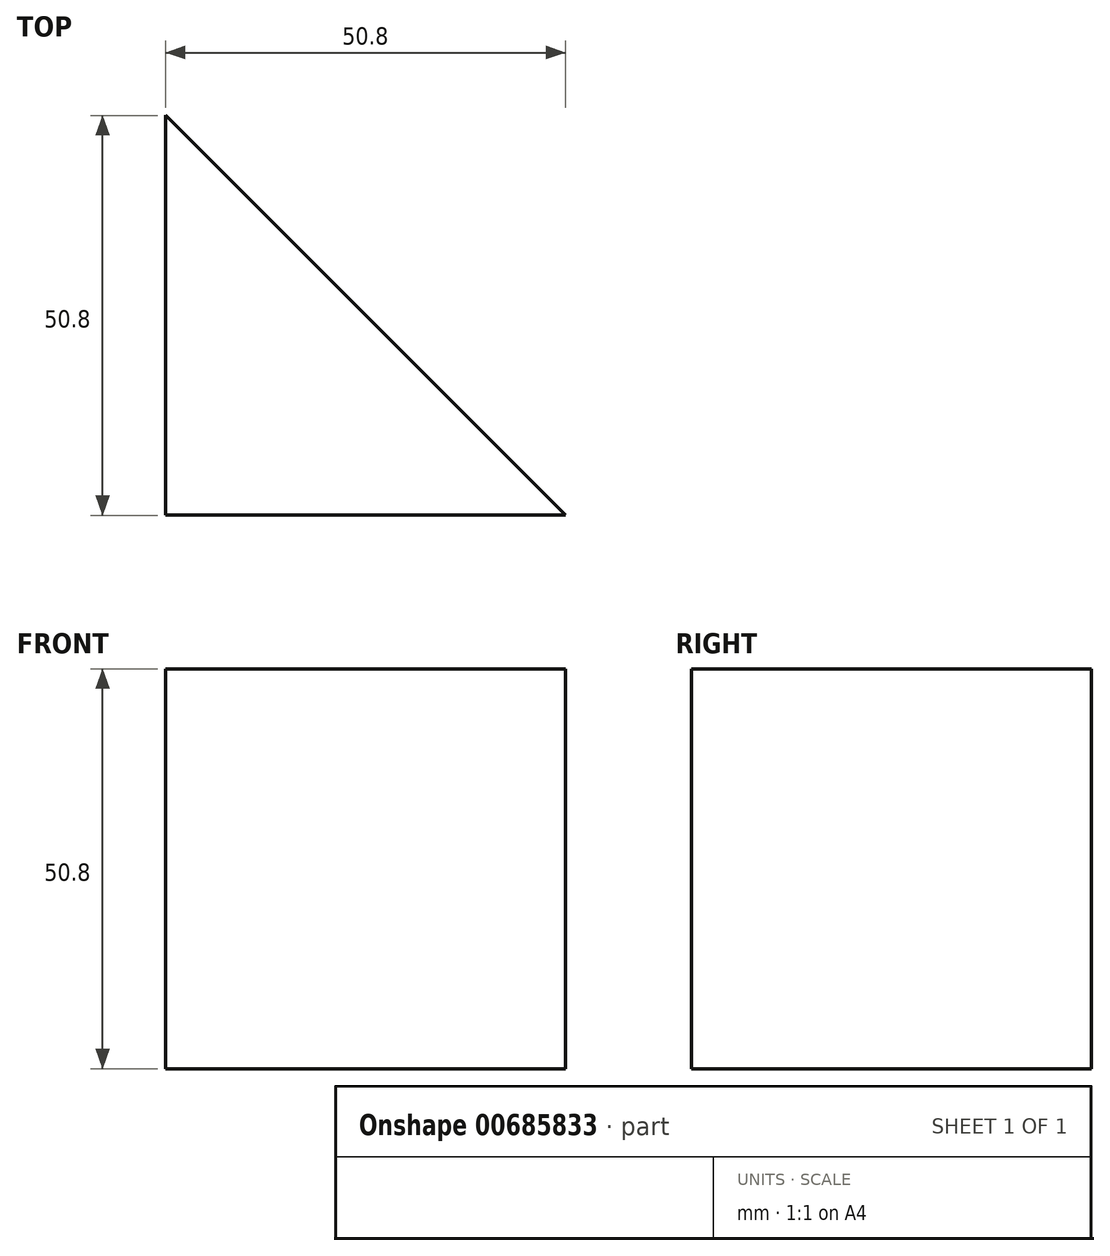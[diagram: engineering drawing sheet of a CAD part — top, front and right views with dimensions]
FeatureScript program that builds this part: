
annotation { "Feature Type Name" : "Feature", "Feature Type Description" : "" }
export const myFeature = defineFeature(function(context is Context, id is Id, definition is map)
    precondition{}
    {
        {
            var Q0;
            Q0=qCreatedBy(makeId("Top.planeOp"),FACE);
            var sketch = newSketch(context, id + "F0", { "sketchPlane" : qUnion([Q0])});
            skLineSegment(sketch, "E0.top", {"start": v(-26.26, -31.75) * mm, "end": v(24.54, -31.75) * mm});
            skLineSegment(sketch, "E0.left", {"start": v(-26.26, 19.05) * mm, "end": v(-26.26, -31.75) * mm});
            skLineSegment(sketch, "E1", {"start": v(-26.26, 19.05) * mm, "end": v(24.54, -31.75) * mm});
            skSolve(sketch);
        }
        {
            var Q0;
            Q0 = qSketchRegion(id + "F0", true);
            extrude(context, id + "F1", {"entities" : qUnion([Q0]), "depth" : 50.8 * mm, "offsetDistance" : 25.4 * mm});
        }
    });
